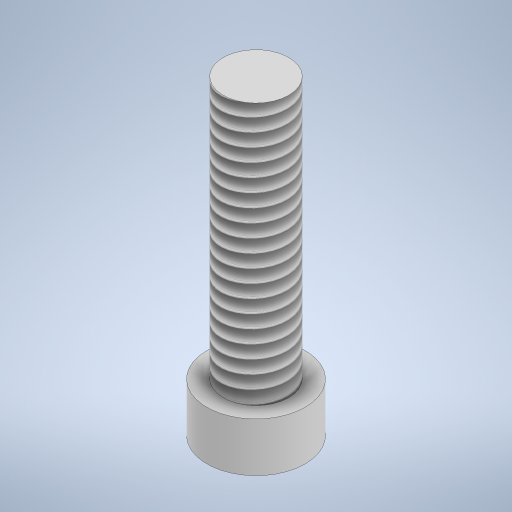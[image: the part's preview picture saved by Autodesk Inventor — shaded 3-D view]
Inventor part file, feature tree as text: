
AUTODESK INVENTOR PART (.ipt)
format: ipt  version: 2024.2 (Build 282272000, 272)  size: 284,160 bytes
history: native  units: mm
features: extrude x2, sketch x2, thread x1
ambient origin geometry x8: Origin, YZ Plane, XZ Plane, XY Plane, X Axis, Y Axis, Z Axis, Center Point
bodies: Solid1 (feature_tree)
feature tree (5):
  extrude  "Extrusion1"  Depth=1.5mm TaperAngle=0.0deg
  extrude  "Extrusion2"  Depth=8.0mm TaperAngle=0.0deg
  thread  "Thread1"  [1 undecoded]
  sketch  "Sketch1"  dims[d0=3.0mm d1=1.5mm d2=0.0mm]
  sketch  "Sketch2"  dims[d3=2.0mm d4=8.0mm d5=0.0mm d6=8.0mm d7=0.0mm]
note: 1 required parameter value undecoded (feature->parameter linkage not recoverable at this tier; creation-order binding heuristic only, values carry confidence <= 0.55)
